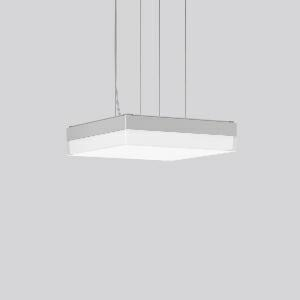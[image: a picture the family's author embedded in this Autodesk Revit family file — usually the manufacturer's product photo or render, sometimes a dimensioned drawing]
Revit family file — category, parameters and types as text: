
# Revit family: flat_slim_square_312542_004_76_9d9a
name_source: partatom
category: Lighting Fixtures
units: mm (PartAtom-declared; Revit-internal decimal feet)

## family parameters
Cut with Voids When Loaded = No
Host = Face
Light Source = No
Part Type = Normal
Room Calculation Point = No
Round Connector Dimension = Use Diameter
Shared = No

## types (1)
- MultiLumen 2 840 (1 x LED Modul 840, 2300 lm, 4000)
    Apparent Load = 21 VA
    CIE Flux Codes = 43 75 93 91 100
    Color Rendering = 80
    Color Temperature = 4000
    Default Elevation = 1800 mm
    Height = 70 mm
    Lamp = 1 x LED Modul 840
    Lamp Light Flux = 2300 lm
    Lamp count = 1
    Length = 300 mm
    Lifetime = 50000 h
    Luminous efficacy = 110 lm/W
    Manufacturer = RZB
    ModVariant = No
    Model = 312542.004.76
    Mounting Place = Ceiling
    Mounting Type = Pendant
    Number of Poles = 1
    OnlyDefault = Yes
    Power Factor = 1
    Product Name = FLAT SLIM square
    Product group = Pendant luminaires
    ProductGroupID = 902
    Protection Class = Protection class I
    Protection Degree = IP 40
    RLX_Detail_Level = 1
    RLX_Emergency_Light_Flux = 0 lm
    RLX_Emergency_Type = 0
    RLX_Emergency_Type_DB = No
    RlxData = <blob elided: 14325 chars, md5=583776bc>
    Socket = socket
    Standby Power = 0 W
    System Light Flux = 2300 lm
    System Power = 21 W
    Type Comments = MultiLumen 2 840
    Type Image = 312542.004.jpg
    URL = http://relux.com
    VarID = multilumen_2_840
    Voltage = 230 V
    Voltage Range = 220-240 V
    Weight = 0.00 kg
    Width = 300 mm

## geometry (parser evidence)
native form markers: Sweep x13
no freeform markers — native parametric forms only
